# Revit family: P190780JX-123c_JEC3536HB_Black_JA_Cooking_Cooktops
name_source: partatom
category: Specialty Equipment
units: mm (PartAtom-declared; Revit-internal decimal feet)

## family parameters
Always vertical = Yes
Cut with Voids When Loaded = No
Enable Cutting in Views = No
Maintain Annotation Orientation = No
Part Type = Normal
Room Calculation Point = No
Round Connector Dimension = Use Diameter
Shared = No
Work Plane-Based = No

## types (1)
- JEC3536HB
    Amps = 0 A
    Body Material = ARCAT - Metal - Steel - Stainless
    Cooktop Material = ARCAT - Glass - Tempered - Black
    Default Elevation = 0"
    Depth = 21 3/4"
    Description = Oblivian Glass 36" Electric Radiant Cooktop
Table de cuisson en verre hypnotisant avec boutons à effet de halo, 36 po
    Family Name = RADIANT UPDRAFT COOKTOP - 36"
    Feature 1 = Triple-Choice™ Element
Élément Triple-Choice™
    Feature 2 = Oblivion Glass Surface
Surface en verre hypnotisant
    Feature 3 = Halo-Effect Knobs
Boutons à effet de halo
    Height = 6 1/16"
    Installation-Fabrication = http://access.whirlpool.com Instruction&sku=JEC3536HB&language=EN
http://access.whirlpool.com Instruction&sku=JEC3536HB&language=EN
    Knob Material = ARCAT - Metal - Steel - Gray
    Manufacturer = Jenn Air
    Model = JEC3536HB
    Voltage = 0 V
    Width = 36 5/16"

## geometry (parser evidence)
native form markers: Sweep x2
no freeform markers — native parametric forms only
